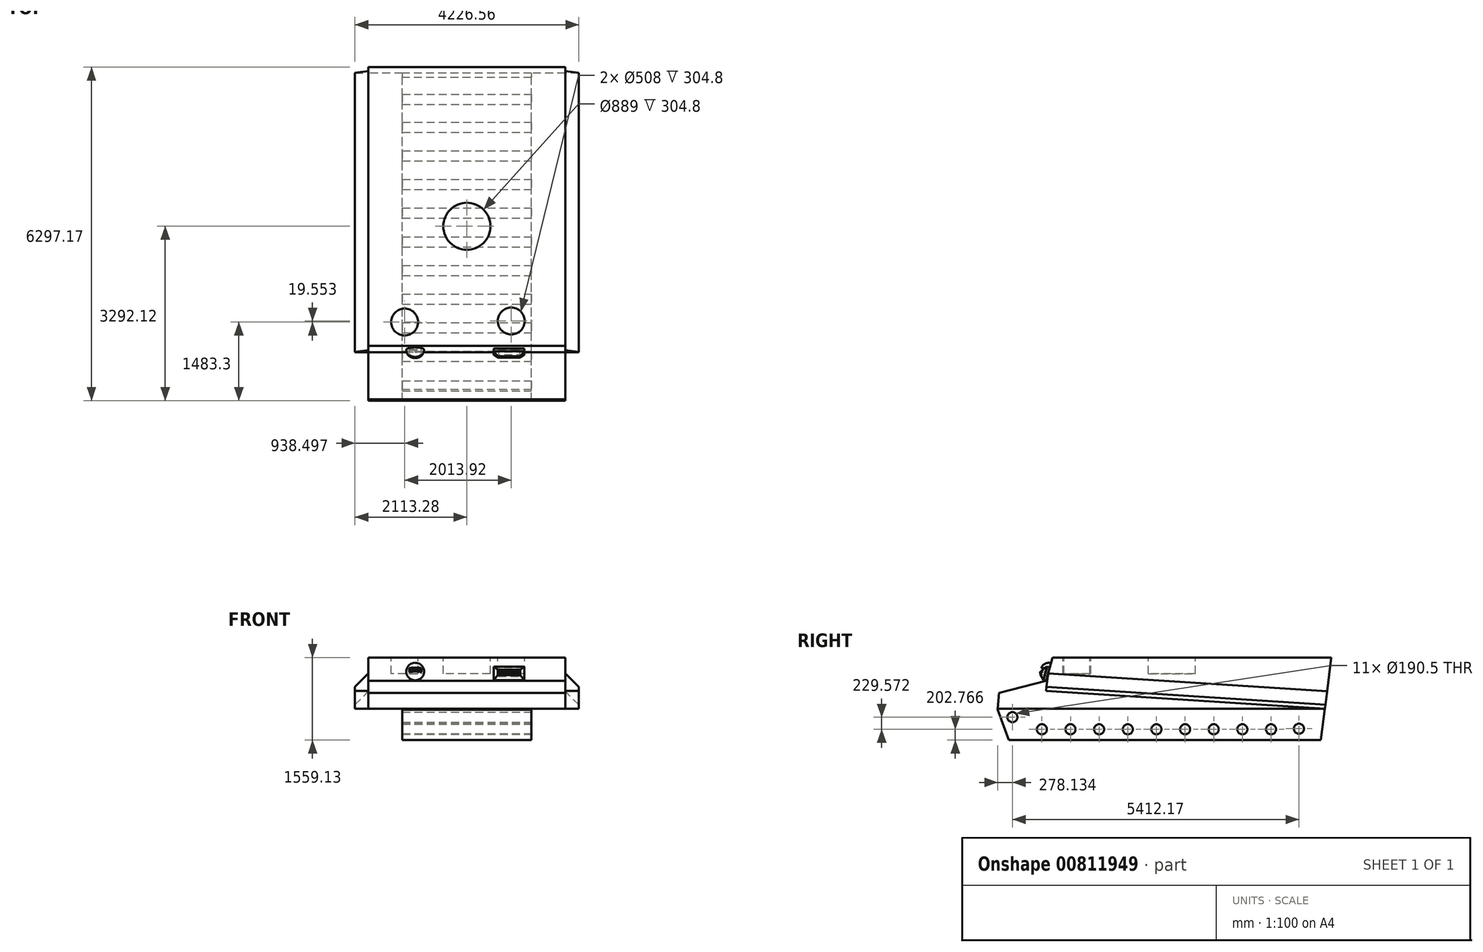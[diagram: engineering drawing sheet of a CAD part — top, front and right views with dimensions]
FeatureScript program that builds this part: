
annotation { "Feature Type Name" : "Feature", "Feature Type Description" : "" }
export const myFeature = defineFeature(function(context is Context, id is Id, definition is map)
    precondition{}
    {
        {
            var Q0;
            Q0=qCreatedBy(makeId("Right.planeOp"),FACE);
            var sketch = newSketch(context, id + "F0", { "sketchPlane" : qUnion([Q0])});
            skLineSegment(sketch, "E0", {"start": v(0, 0) * mm, "end": v(26.57, 303.64) * mm});
            skLineSegment(sketch, "E1", {"start": v(26.57, 303.64) * mm, "end": v(912.57, 529.75) * mm});
            skLineSegment(sketch, "E2", {"start": v(912.57, 529.75) * mm, "end": v(1036.16, 969.93) * mm});
            skLineSegment(sketch, "E3", {"start": v(1036.16, 969.93) * mm, "end": v(4846.16, 969.93) * mm});
            skLineSegment(sketch, "E4", {"start": v(0, 0) * mm, "end": v(6181.27, 0) * mm});
            skLineSegment(sketch, "E5", {"start": v(6297.17, 965.94) * mm, "end": v(6181.27, 0) * mm});
            skLineSegment(sketch, "E6", {"start": v(6297.17, 965.94) * mm, "end": v(4846.16, 969.93) * mm});
            skSolve(sketch);
        }
        {
            var Q0;
            Q0 = qSketchRegion(id + "F0", true);
            extrude(context, id + "F1", {"entities" : qUnion([Q0]), "depth" : 1859.28 * mm, "offsetDistance" : 25.4 * mm, "hasSecondDirection" : true, "secondDirectionOppositeDirection" : true, "secondDirectionDepth" : 1859.28 * mm});
        }
        {
            var Q0;
            Q0=qCreatedBy(makeId("Right.planeOp"),FACE);
            var sketch = newSketch(context, id + "F2", { "sketchPlane" : qUnion([Q0])});
            skLineSegment(sketch, "E7", {"start": v(0, -16.36) * mm, "end": v(208.5, -589.2) * mm});
            skLineSegment(sketch, "E8", {"start": v(0, -16.36) * mm, "end": v(0, 0) * mm});
            skLineSegment(sketch, "E9", {"start": v(0, 0) * mm, "end": v(6181.41, 0) * mm});
            skLineSegment(sketch, "E10", {"start": v(6181.41, 0) * mm, "end": v(6102.94, -589.2) * mm});
            skLineSegment(sketch, "E11", {"start": v(208.5, -589.2) * mm, "end": v(6102.94, -589.2) * mm});
            skSolve(sketch);
        }
        {
            var Q0;
            Q0 = qSketchRegion(id + "F2", true);
            extrude(context, id + "F3", {"entities" : qUnion([Q0]), "operationType" : NewBodyOperationType.ADD, "depth" : 1219.2 * mm, "offsetDistance" : 25.4 * mm, "hasSecondDirection" : true, "secondDirectionOppositeDirection" : true, "secondDirectionDepth" : 1219.2 * mm});
        }
        {
            var Q0;
            Q0=makeQuery(id+"F1.opExtrude","SWEPT_FACE",FACE,{"disambiguationData":[OSD([sQuery(id+"F0.wireOp",EDGE,"E2")])]});
            var sketch = newSketch(context, id + "F4", { "sketchPlane" : qUnion([Q0])});
            skCircle(sketch, "E12", {"center": v(-976.12, 934.62) * mm, "radius": 169.02 * mm});
            skSolve(sketch);
        }
        {
            var Q0;
            Q0 = qSketchRegion(id + "F4", true);
            extrude(context, id + "F5", {"entities" : qUnion([Q0]), "operationType" : NewBodyOperationType.ADD, "depth" : 152.4 * mm, "offsetDistance" : 25.4 * mm});
        }
        {
            var Q0;
            Q0=makeQuery(id+"F5.opExtrude","CAP_EDGE",EDGE,{"disambiguationData":[OSD([sQuery(id+"F4.wireOp",EDGE,"E12")])],"isStart":false});
            fillet(context, id + "F6", {"entities" : qUnion([Q0]), "radius" : 152.4 * mm, "tangentPropagation" : true, "allowEdgeOverflow" : false});
        }
        {
            var Q0;
            Q0=makeQuery(id+"F1.opExtrude","SWEPT_FACE",FACE,{"disambiguationData":[OSD([sQuery(id+"F0.wireOp",EDGE,"E2")])]});
            var sketch = newSketch(context, id + "F7", { "sketchPlane" : qUnion([Q0])});
            skLineSegment(sketch, "E13.bottom", {"start": v(-1086.63, 896.36) * mm, "end": v(-858.92, 896.36) * mm});
            skLineSegment(sketch, "E13.top", {"start": v(-1086.63, 972.88) * mm, "end": v(-858.92, 972.88) * mm});
            skLineSegment(sketch, "E13.left", {"start": v(-1086.63, 896.36) * mm, "end": v(-1086.63, 972.88) * mm});
            skLineSegment(sketch, "E13.right", {"start": v(-858.92, 896.36) * mm, "end": v(-858.92, 972.88) * mm});
            skSolve(sketch);
        }
        {
            var Q0;
            Q0 = qSketchRegion(id + "F7", true);
            extrude(context, id + "F8", {"entities" : qUnion([Q0]), "operationType" : NewBodyOperationType.REMOVE, "depth" : 609.6 * mm, "offsetDistance" : 25.4 * mm});
        }
        {
            var Q0;
            Q0=makeQuery(id+"F1.opExtrude","SWEPT_FACE",FACE,{"disambiguationData":[OSD([sQuery(id+"F0.wireOp",EDGE,"E2")])]});
            var sketch = newSketch(context, id + "F9", { "sketchPlane" : qUnion([Q0])});
            skLineSegment(sketch, "E14.bottom", {"start": v(1088.1, 756.72) * mm, "end": v(506.68, 756.72) * mm});
            skLineSegment(sketch, "E14.top", {"start": v(1088.1, 1016.63) * mm, "end": v(506.68, 1016.63) * mm});
            skLineSegment(sketch, "E14.left", {"start": v(1088.1, 756.72) * mm, "end": v(1088.1, 1016.63) * mm});
            skLineSegment(sketch, "E14.right", {"start": v(506.68, 756.72) * mm, "end": v(506.68, 1016.63) * mm});
            skSolve(sketch);
        }
        {
            var Q0;
            Q0 = qSketchRegion(id + "F9", true);
            extrude(context, id + "F10", {"entities" : qUnion([Q0]), "operationType" : NewBodyOperationType.ADD, "depth" : 127 * mm, "offsetDistance" : 25.4 * mm});
        }
        {
            var Q0;
            Q0=makeQuery(id+"F10.opExtrude","CAP_EDGE",EDGE,{"disambiguationData":[OSD([sQuery(id+"F9.wireOp",EDGE,"E14.top")])],"isStart":false});
            var Q1;
            Q1=makeQuery(id+"F10.opExtrude","CAP_EDGE",EDGE,{"disambiguationData":[OSD([sQuery(id+"F9.wireOp",EDGE,"E14.left")])],"isStart":false});
            var Q2;
            Q2=makeQuery(id+"F10.opExtrude","CAP_EDGE",EDGE,{"disambiguationData":[OSD([sQuery(id+"F9.wireOp",EDGE,"E14.bottom")])],"isStart":false});
            var Q3;
            Q3=makeQuery(id+"F10.opExtrude","CAP_EDGE",EDGE,{"disambiguationData":[OSD([sQuery(id+"F9.wireOp",EDGE,"E14.right")])],"isStart":false});
            chamfer(context, id + "F11", {"entities" : qUnion([Q0, Q1, Q2, Q3]), "width" : 76.2 * mm, "tangentPropagation" : true});
        }
        {
            var Q0;
            Q0=makeQuery(id+"F10.opExtrude","CAP_FACE",FACE,{"disambiguationData":[OSD([sQuery(id+"F9.wireOp",EDGE,"E14.bottom"),sQuery(id+"F9.wireOp",EDGE,"E14.top"),sQuery(id+"F9.wireOp",EDGE,"E14.left"),sQuery(id+"F9.wireOp",EDGE,"E14.right")])],"isStart":false});
            var sketch = newSketch(context, id + "F12", { "sketchPlane" : qUnion([Q0])});
            skLineSegment(sketch, "E15.bottom", {"start": v(594.67, 849.4) * mm, "end": v(997.37, 849.4) * mm});
            skLineSegment(sketch, "E15.top", {"start": v(594.67, 921.63) * mm, "end": v(997.37, 921.63) * mm});
            skLineSegment(sketch, "E15.left", {"start": v(594.67, 849.4) * mm, "end": v(594.67, 921.63) * mm});
            skLineSegment(sketch, "E15.right", {"start": v(997.37, 849.4) * mm, "end": v(997.37, 921.63) * mm});
            skSolve(sketch);
        }
        {
            var Q0;
            Q0 = qSketchRegion(id + "F12", true);
            extrude(context, id + "F13", {"entities" : qUnion([Q0]), "operationType" : NewBodyOperationType.REMOVE, "oppositeDirection" : true, "depth" : 152.4 * mm, "offsetDistance" : 25.4 * mm});
        }
        {
            var Q0;
            Q0=makeQuery(id+"F1.opExtrude","SWEPT_FACE",FACE,{"disambiguationData":[OSD([sQuery(id+"F0.wireOp",EDGE,"E3")])]});
            var sketch = newSketch(context, id + "F14", { "sketchPlane" : qUnion([Q0])});
            skCircle(sketch, "E16", {"center": v(-1174.78, 1483.3) * mm, "radius": 254 * mm});
            skCircle(sketch, "E17", {"center": v(839.13, 1502.85) * mm, "radius": 254 * mm});
            skSolve(sketch);
        }
        {
            var Q0;
            Q0 = qSketchRegion(id + "F14", true);
            extrude(context, id + "F15", {"entities" : qUnion([Q0]), "operationType" : NewBodyOperationType.REMOVE, "oppositeDirection" : true, "depth" : 304.8 * mm, "offsetDistance" : 25.4 * mm});
        }
        {
            var Q0;
            Q0=makeQuery(id+"F1.opExtrude","SWEPT_FACE",FACE,{"disambiguationData":[OSD([sQuery(id+"F0.wireOp",EDGE,"E3")])]});
            var sketch = newSketch(context, id + "F16", { "sketchPlane" : qUnion([Q0])});
            skCircle(sketch, "E18", {"center": v(0, 3292.12) * mm, "radius": 444.5 * mm});
            skSolve(sketch);
        }
        {
            var Q0;
            Q0 = qSketchRegion(id + "F16", true);
            extrude(context, id + "F17", {"entities" : qUnion([Q0]), "operationType" : NewBodyOperationType.REMOVE, "oppositeDirection" : true, "depth" : 304.8 * mm, "offsetDistance" : 25.4 * mm});
        }
        {
            var Q0;
            Q0=makeQuery(id+"F1.opExtrude","CAP_FACE",FACE,{"disambiguationData":[OSD([sQuery(id+"F0.wireOp",EDGE,"E0"),sQuery(id+"F0.wireOp",EDGE,"E1"),sQuery(id+"F0.wireOp",EDGE,"E2"),sQuery(id+"F0.wireOp",EDGE,"E3"),sQuery(id+"F0.wireOp",EDGE,"E4"),sQuery(id+"F0.wireOp",EDGE,"E5"),sQuery(id+"F0.wireOp",EDGE,"E6")])],"isStart":false});
            var sketch = newSketch(context, id + "F18", { "sketchPlane" : qUnion([Q0])});
            skLineSegment(sketch, "E19", {"start": v(951.86, 669.68) * mm, "end": v(6220.86, 329.99) * mm});
            skLineSegment(sketch, "E20", {"start": v(6220.86, 329.99) * mm, "end": v(6181.27, 0) * mm});
            skLineSegment(sketch, "E21", {"start": v(6181.27, 0) * mm, "end": v(912.57, 339.68) * mm});
            skLineSegment(sketch, "E22", {"start": v(912.57, 339.68) * mm, "end": v(951.86, 669.68) * mm});
            skSolve(sketch);
        }
        {
            var Q0;
            Q0 = qSketchRegion(id + "F18", true);
            extrude(context, id + "F19", {"entities" : qUnion([Q0]), "operationType" : NewBodyOperationType.ADD, "depth" : 254 * mm, "offsetDistance" : 25.4 * mm});
        }
        {
            var Q0;
            Q0=makeQuery(id+"F19.opExtrude","CAP_EDGE",EDGE,{"disambiguationData":[OSD([sQuery(id+"F18.wireOp",EDGE,"E19")])],"isStart":false});
            chamfer(context, id + "F20", {"entities" : qUnion([Q0]), "width" : 254 * mm, "tangentPropagation" : true});
        }
        {
            var Q0;
            Q0=makeQuery(id+"F1.opExtrude","CAP_FACE",FACE,{"disambiguationData":[OSD([sQuery(id+"F0.wireOp",EDGE,"E0"),sQuery(id+"F0.wireOp",EDGE,"E1"),sQuery(id+"F0.wireOp",EDGE,"E2"),sQuery(id+"F0.wireOp",EDGE,"E3"),sQuery(id+"F0.wireOp",EDGE,"E4"),sQuery(id+"F0.wireOp",EDGE,"E5"),sQuery(id+"F0.wireOp",EDGE,"E6")])],"isStart":true});
            var sketch = newSketch(context, id + "F21", { "sketchPlane" : qUnion([Q0])});
            skLineSegment(sketch, "E23", {"start": v(-6181.27, 0) * mm, "end": v(-912.57, 339.77) * mm});
            skLineSegment(sketch, "E24", {"start": v(-912.57, 339.77) * mm, "end": v(-951.88, 669.77) * mm});
            skLineSegment(sketch, "E25", {"start": v(-6181.27, 0) * mm, "end": v(-6260.45, 659.96) * mm});
            skLineSegment(sketch, "E26", {"start": v(-951.88, 669.77) * mm, "end": v(-6220.86, 329.98) * mm});
            skSolve(sketch);
        }
        {
            var Q0;
            {var subQ0=sQuery(id+"F21.wireOp",EDGE,"E23");Q0=makeQuery(id+"F21.imprint","IMPRINT",FACE,{"disambiguationData":[TD([[makeQuery(id+"F21.imprint","IMPRINT",EDGE,{"derivedFrom":subQ0}),1.0]])]});}
            extrude(context, id + "F22", {"entities" : qUnion([Q0]), "operationType" : NewBodyOperationType.ADD, "depth" : 254 * mm, "offsetDistance" : 25.4 * mm});
        }
        {
            var Q0;
            Q0=makeQuery(id+"F22.opExtrude","CAP_EDGE",EDGE,{"disambiguationData":[OSD([sQuery(id+"F21.wireOp",EDGE,"E26")])],"isStart":false});
            chamfer(context, id + "F23", {"entities" : qUnion([Q0]), "width" : 254 * mm, "tangentPropagation" : true});
        }
        {
            var Q0;
            Q0=makeQuery(id+"F3.opExtrude","CAP_FACE",FACE,{"disambiguationData":[OSD([sQuery(id+"F2.wireOp",EDGE,"E7"),sQuery(id+"F2.wireOp",EDGE,"E8"),sQuery(id+"F2.wireOp",EDGE,"E9"),sQuery(id+"F2.wireOp",EDGE,"E10"),sQuery(id+"F2.wireOp",EDGE,"E11")])],"isStart":false});
            var sketch = newSketch(context, id + "F24", { "sketchPlane" : qUnion([Q0])});
            skCircle(sketch, "E27", {"center": v(278.13, -156.86) * mm, "radius": 95.25 * mm});
            skCircle(sketch, "E28", {"center": v(5690.3, -374.96) * mm, "radius": 95.25 * mm});
            skCircle(sketch, "E29", {"center": v(834.85, -386.43) * mm, "radius": 95.25 * mm});
            skCircle(sketch, "E30.1.0.0", {"center": v(1375.87, -386.43) * mm, "radius": 95.25 * mm});
            skCircle(sketch, "E30.2.0.0", {"center": v(1916.89, -386.43) * mm, "radius": 95.25 * mm});
            skCircle(sketch, "E30.3.0.0", {"center": v(2457.9, -386.43) * mm, "radius": 95.25 * mm});
            skCircle(sketch, "E30.4.0.0", {"center": v(2998.93, -386.43) * mm, "radius": 95.25 * mm});
            skCircle(sketch, "E30.5.0.0", {"center": v(3539.95, -386.43) * mm, "radius": 95.25 * mm});
            skCircle(sketch, "E30.6.0.0", {"center": v(4080.97, -386.43) * mm, "radius": 95.25 * mm});
            skCircle(sketch, "E30.7.0.0", {"center": v(4621.99, -386.43) * mm, "radius": 95.25 * mm});
            skCircle(sketch, "E30.8.0.0", {"center": v(5163, -386.43) * mm, "radius": 95.25 * mm});
            skLineSegment(sketch, "E30.direction1", {"start": v(834.85, -386.43) * mm, "end": v(1375.87, -386.43) * mm, "construction": true});
            skSolve(sketch);
        }
        {
            var Q0;
            Q0=makeQuery(id+"F24.imprint","IMPRINT",FACE,{"disambiguationData":[TD([[makeQuery(id+"F24.imprint","IMPRINT",EDGE,{"derivedFrom":sQuery(id+"F24.wireOp",EDGE,"E27")}),1.0]])]});
            var Q1;
            Q1=makeQuery(id+"F24.imprint","IMPRINT",FACE,{"disambiguationData":[TD([[makeQuery(id+"F24.imprint","IMPRINT",EDGE,{"derivedFrom":sQuery(id+"F24.wireOp",EDGE,"E29")}),1.0]])]});
            var Q2;
            Q2=makeQuery(id+"F24.imprint","IMPRINT",FACE,{"disambiguationData":[TD([[makeQuery(id+"F24.imprint","IMPRINT",EDGE,{"derivedFrom":sQuery(id+"F24.wireOp",EDGE,"E30.1.0.0")}),1.0]])]});
            var Q3;
            Q3=makeQuery(id+"F24.imprint","IMPRINT",FACE,{"disambiguationData":[TD([[makeQuery(id+"F24.imprint","IMPRINT",EDGE,{"derivedFrom":sQuery(id+"F24.wireOp",EDGE,"E30.2.0.0")}),1.0]])]});
            var Q4;
            Q4=makeQuery(id+"F24.imprint","IMPRINT",FACE,{"disambiguationData":[TD([[makeQuery(id+"F24.imprint","IMPRINT",EDGE,{"derivedFrom":sQuery(id+"F24.wireOp",EDGE,"E30.3.0.0")}),1.0]])]});
            var Q5;
            Q5=makeQuery(id+"F24.imprint","IMPRINT",FACE,{"disambiguationData":[TD([[makeQuery(id+"F24.imprint","IMPRINT",EDGE,{"derivedFrom":sQuery(id+"F24.wireOp",EDGE,"E30.4.0.0")}),1.0]])]});
            var Q6;
            Q6=makeQuery(id+"F24.imprint","IMPRINT",FACE,{"disambiguationData":[TD([[makeQuery(id+"F24.imprint","IMPRINT",EDGE,{"derivedFrom":sQuery(id+"F24.wireOp",EDGE,"E30.5.0.0")}),1.0]])]});
            var Q7;
            Q7=makeQuery(id+"F24.imprint","IMPRINT",FACE,{"disambiguationData":[TD([[makeQuery(id+"F24.imprint","IMPRINT",EDGE,{"derivedFrom":sQuery(id+"F24.wireOp",EDGE,"E30.6.0.0")}),1.0]])]});
            var Q8;
            Q8=makeQuery(id+"F24.imprint","IMPRINT",FACE,{"disambiguationData":[TD([[makeQuery(id+"F24.imprint","IMPRINT",EDGE,{"derivedFrom":sQuery(id+"F24.wireOp",EDGE,"E30.7.0.0")}),1.0]])]});
            var Q9;
            Q9=makeQuery(id+"F24.imprint","IMPRINT",FACE,{"disambiguationData":[TD([[makeQuery(id+"F24.imprint","IMPRINT",EDGE,{"derivedFrom":sQuery(id+"F24.wireOp",EDGE,"E30.8.0.0")}),1.0]])]});
            var Q10;
            Q10=makeQuery(id+"F24.imprint","IMPRINT",FACE,{"disambiguationData":[TD([[makeQuery(id+"F24.imprint","IMPRINT",EDGE,{"derivedFrom":sQuery(id+"F24.wireOp",EDGE,"E28")}),1.0]])]});
            extrude(context, id + "F25", {"entities" : qUnion([Q0, Q1, Q2, Q3, Q4, Q5, Q6, Q7, Q8, Q9, Q10]), "operationType" : NewBodyOperationType.REMOVE, "oppositeDirection" : true, "depth" : 3048 * mm, "offsetDistance" : 25.4 * mm});
        }
    });
